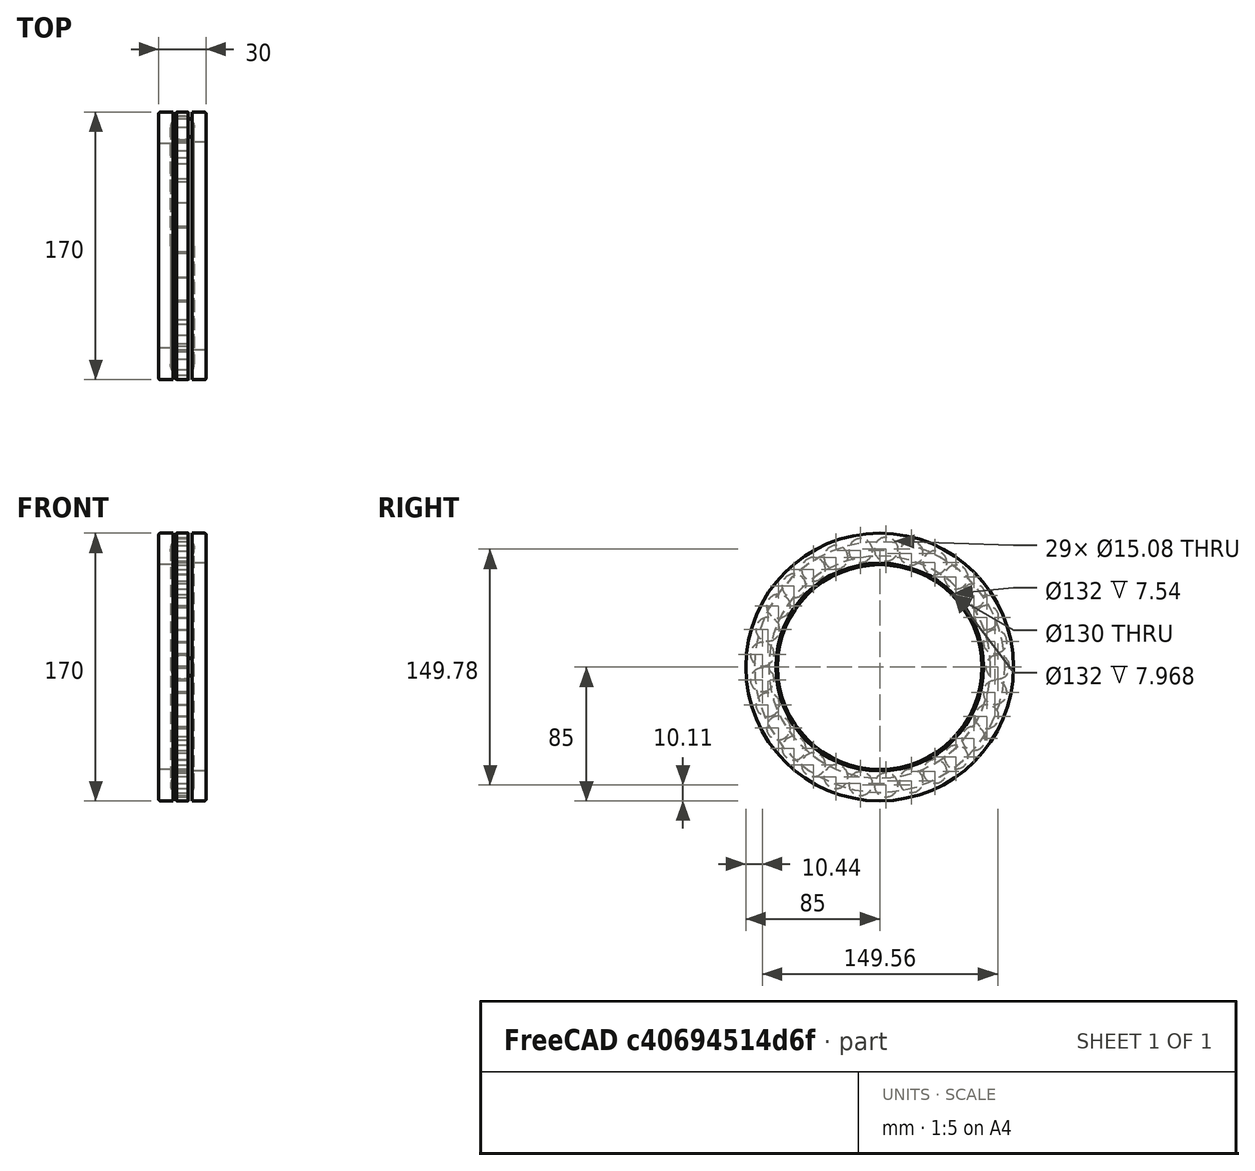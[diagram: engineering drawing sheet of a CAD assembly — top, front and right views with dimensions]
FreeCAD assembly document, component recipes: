
FREECAD ASSEMBLY — COMPONENT RECIPES ("lozysko 51126")

This assembly document has 28 components, labeled P0..P27 below (a component is one placed body or linked part). 0 of them carry a construction recipe — the FreeCAD feature program that regenerates the part from scratch, quoted from this document or its linked companion documents; the rest are supplied as boundary geometry only. No exploded tour is included for this assembly.
COMPONENT P0 — geometry summary ("_51126_PART005"; no construction recipe available for this part):
  bounding box: 15.1 x 15.1 x 15.1 mm
  tessellated surface: 8,032 triangles
  volume: 1796 mm^3 (52% of its bounding box)
  symmetry: revolution-symmetric about the x axis through its bounding-box center; revolution-symmetric about the y axis through its bounding-box center; revolution-symmetric about the z axis through its bounding-box center; mirror-symmetric across its x mid-plane, y mid-plane, z mid-plane
COMPONENT P1 — geometry summary ("_51126_PART006"; no construction recipe available for this part):
  bounding box: 15.1 x 15.1 x 15.1 mm
  tessellated surface: 8,032 triangles
  volume: 1796 mm^3 (52% of its bounding box)
  symmetry: revolution-symmetric about the x axis through its bounding-box center; revolution-symmetric about the y axis through its bounding-box center; revolution-symmetric about the z axis through its bounding-box center; mirror-symmetric across its x mid-plane, y mid-plane, z mid-plane
COMPONENT P2 — geometry summary ("_51126_PART007"; no construction recipe available for this part):
  bounding box: 15.1 x 15.1 x 15.1 mm
  tessellated surface: 8,032 triangles
  volume: 1796 mm^3 (52% of its bounding box)
  symmetry: revolution-symmetric about the x axis through its bounding-box center; revolution-symmetric about the y axis through its bounding-box center; revolution-symmetric about the z axis through its bounding-box center; mirror-symmetric across its x mid-plane, y mid-plane, z mid-plane
COMPONENT P3 — geometry summary ("_51126_PART008"; no construction recipe available for this part):
  bounding box: 15.1 x 15.1 x 15.1 mm
  tessellated surface: 8,032 triangles
  volume: 1796 mm^3 (52% of its bounding box)
  symmetry: revolution-symmetric about the x axis through its bounding-box center; revolution-symmetric about the y axis through its bounding-box center; revolution-symmetric about the z axis through its bounding-box center; mirror-symmetric across its x mid-plane, y mid-plane, z mid-plane
COMPONENT P4 — geometry summary ("_51126_PART009"; no construction recipe available for this part):
  bounding box: 15.1 x 15.1 x 15.1 mm
  tessellated surface: 8,032 triangles
  volume: 1796 mm^3 (52% of its bounding box)
  symmetry: revolution-symmetric about the x axis through its bounding-box center; revolution-symmetric about the y axis through its bounding-box center; revolution-symmetric about the z axis through its bounding-box center; mirror-symmetric across its x mid-plane, y mid-plane, z mid-plane
COMPONENT P5 — geometry summary ("_51126_PART010"; no construction recipe available for this part):
  bounding box: 15.1 x 15.1 x 15.1 mm
  tessellated surface: 8,032 triangles
  volume: 1796 mm^3 (52% of its bounding box)
  symmetry: revolution-symmetric about the x axis through its bounding-box center; revolution-symmetric about the y axis through its bounding-box center; revolution-symmetric about the z axis through its bounding-box center; mirror-symmetric across its x mid-plane, y mid-plane, z mid-plane
COMPONENT P6 — geometry summary ("_51126_PART011"; no construction recipe available for this part):
  bounding box: 15.1 x 15.1 x 15.1 mm
  tessellated surface: 8,032 triangles
  volume: 1796 mm^3 (52% of its bounding box)
  symmetry: revolution-symmetric about the x axis through its bounding-box center; revolution-symmetric about the y axis through its bounding-box center; revolution-symmetric about the z axis through its bounding-box center; mirror-symmetric across its x mid-plane, y mid-plane, z mid-plane
COMPONENT P7 — geometry summary ("_51126_PART012"; no construction recipe available for this part):
  bounding box: 15.1 x 15.1 x 15.1 mm
  tessellated surface: 8,032 triangles
  volume: 1796 mm^3 (52% of its bounding box)
  symmetry: revolution-symmetric about the x axis through its bounding-box center; revolution-symmetric about the y axis through its bounding-box center; revolution-symmetric about the z axis through its bounding-box center; mirror-symmetric across its x mid-plane, y mid-plane, z mid-plane
COMPONENT P8 — geometry summary ("_51126_PART013"; no construction recipe available for this part):
  bounding box: 15.1 x 15.1 x 15.1 mm
  tessellated surface: 8,032 triangles
  volume: 1796 mm^3 (52% of its bounding box)
  symmetry: revolution-symmetric about the x axis through its bounding-box center; revolution-symmetric about the y axis through its bounding-box center; revolution-symmetric about the z axis through its bounding-box center; mirror-symmetric across its x mid-plane, y mid-plane, z mid-plane
COMPONENT P9 — geometry summary ("_51126_PART014"; no construction recipe available for this part):
  bounding box: 15.1 x 15.1 x 15.1 mm
  tessellated surface: 8,032 triangles
  volume: 1796 mm^3 (52% of its bounding box)
  symmetry: revolution-symmetric about the x axis through its bounding-box center; revolution-symmetric about the y axis through its bounding-box center; revolution-symmetric about the z axis through its bounding-box center; mirror-symmetric across its x mid-plane, y mid-plane, z mid-plane
COMPONENT P10 — geometry summary ("_51126_PART015"; no construction recipe available for this part):
  bounding box: 15.1 x 15.1 x 15.1 mm
  tessellated surface: 8,032 triangles
  volume: 1796 mm^3 (52% of its bounding box)
  symmetry: revolution-symmetric about the x axis through its bounding-box center; revolution-symmetric about the y axis through its bounding-box center; revolution-symmetric about the z axis through its bounding-box center; mirror-symmetric across its x mid-plane, y mid-plane, z mid-plane
COMPONENT P11 — geometry summary ("_51126_PART016"; no construction recipe available for this part):
  bounding box: 15.1 x 15.1 x 15.1 mm
  tessellated surface: 8,032 triangles
  volume: 1796 mm^3 (52% of its bounding box)
  symmetry: revolution-symmetric about the x axis through its bounding-box center; revolution-symmetric about the y axis through its bounding-box center; revolution-symmetric about the z axis through its bounding-box center; mirror-symmetric across its x mid-plane, y mid-plane, z mid-plane
COMPONENT P12 — geometry summary ("_51126_PART017"; no construction recipe available for this part):
  bounding box: 15.1 x 15.1 x 15.1 mm
  tessellated surface: 8,032 triangles
  volume: 1796 mm^3 (52% of its bounding box)
  symmetry: revolution-symmetric about the x axis through its bounding-box center; revolution-symmetric about the y axis through its bounding-box center; revolution-symmetric about the z axis through its bounding-box center; mirror-symmetric across its x mid-plane, y mid-plane, z mid-plane
COMPONENT P13 — geometry summary ("_51126_PART018"; no construction recipe available for this part):
  bounding box: 15.1 x 15.1 x 15.1 mm
  tessellated surface: 8,032 triangles
  volume: 1796 mm^3 (52% of its bounding box)
  symmetry: revolution-symmetric about the x axis through its bounding-box center; revolution-symmetric about the y axis through its bounding-box center; revolution-symmetric about the z axis through its bounding-box center; mirror-symmetric across its x mid-plane, y mid-plane, z mid-plane
COMPONENT P14 — geometry summary ("_51126_PART019"; no construction recipe available for this part):
  bounding box: 15.1 x 15.1 x 15.1 mm
  tessellated surface: 8,032 triangles
  volume: 1796 mm^3 (52% of its bounding box)
  symmetry: revolution-symmetric about the x axis through its bounding-box center; revolution-symmetric about the y axis through its bounding-box center; revolution-symmetric about the z axis through its bounding-box center; mirror-symmetric across its x mid-plane, y mid-plane, z mid-plane
COMPONENT P15 — geometry summary ("_51126_PART020"; no construction recipe available for this part):
  bounding box: 15.1 x 15.1 x 15.1 mm
  tessellated surface: 8,032 triangles
  volume: 1796 mm^3 (52% of its bounding box)
  symmetry: revolution-symmetric about the x axis through its bounding-box center; revolution-symmetric about the y axis through its bounding-box center; revolution-symmetric about the z axis through its bounding-box center; mirror-symmetric across its x mid-plane, y mid-plane, z mid-plane
COMPONENT P16 — geometry summary ("_51126_PART021"; no construction recipe available for this part):
  bounding box: 15.1 x 15.1 x 15.1 mm
  tessellated surface: 8,032 triangles
  volume: 1796 mm^3 (52% of its bounding box)
  symmetry: revolution-symmetric about the x axis through its bounding-box center; revolution-symmetric about the y axis through its bounding-box center; revolution-symmetric about the z axis through its bounding-box center; mirror-symmetric across its x mid-plane, y mid-plane, z mid-plane
COMPONENT P17 — geometry summary ("_51126_PART022"; no construction recipe available for this part):
  bounding box: 15.1 x 15.1 x 15.1 mm
  tessellated surface: 8,032 triangles
  volume: 1796 mm^3 (52% of its bounding box)
  symmetry: revolution-symmetric about the x axis through its bounding-box center; revolution-symmetric about the y axis through its bounding-box center; revolution-symmetric about the z axis through its bounding-box center; mirror-symmetric across its x mid-plane, y mid-plane, z mid-plane
COMPONENT P18 — geometry summary ("_51126_PART023"; no construction recipe available for this part):
  bounding box: 15.1 x 15.1 x 15.1 mm
  tessellated surface: 8,032 triangles
  volume: 1796 mm^3 (52% of its bounding box)
  symmetry: revolution-symmetric about the x axis through its bounding-box center; revolution-symmetric about the y axis through its bounding-box center; revolution-symmetric about the z axis through its bounding-box center; mirror-symmetric across its x mid-plane, y mid-plane, z mid-plane
COMPONENT P19 — geometry summary ("_51126_PART024"; no construction recipe available for this part):
  bounding box: 15.1 x 15.1 x 15.1 mm
  tessellated surface: 8,032 triangles
  volume: 1796 mm^3 (52% of its bounding box)
  symmetry: revolution-symmetric about the x axis through its bounding-box center; revolution-symmetric about the y axis through its bounding-box center; revolution-symmetric about the z axis through its bounding-box center; mirror-symmetric across its x mid-plane, y mid-plane, z mid-plane
COMPONENT P20 — geometry summary ("_51126_PART025"; no construction recipe available for this part):
  bounding box: 15.1 x 15.1 x 15.1 mm
  tessellated surface: 8,032 triangles
  volume: 1796 mm^3 (52% of its bounding box)
  symmetry: revolution-symmetric about the x axis through its bounding-box center; revolution-symmetric about the y axis through its bounding-box center; revolution-symmetric about the z axis through its bounding-box center; mirror-symmetric across its x mid-plane, y mid-plane, z mid-plane
COMPONENT P21 — geometry summary ("_51126_PART026"; no construction recipe available for this part):
  bounding box: 15.1 x 15.1 x 15.1 mm
  tessellated surface: 8,032 triangles
  volume: 1796 mm^3 (52% of its bounding box)
  symmetry: revolution-symmetric about the x axis through its bounding-box center; revolution-symmetric about the y axis through its bounding-box center; revolution-symmetric about the z axis through its bounding-box center; mirror-symmetric across its x mid-plane, y mid-plane, z mid-plane
COMPONENT P22 — geometry summary ("_51126_PART027"; no construction recipe available for this part):
  bounding box: 15.1 x 15.1 x 15.1 mm
  tessellated surface: 8,032 triangles
  volume: 1796 mm^3 (52% of its bounding box)
  symmetry: revolution-symmetric about the x axis through its bounding-box center; revolution-symmetric about the y axis through its bounding-box center; revolution-symmetric about the z axis through its bounding-box center; mirror-symmetric across its x mid-plane, y mid-plane, z mid-plane
COMPONENT P23 — geometry summary ("_51126_PART028"; no construction recipe available for this part):
  bounding box: 15.1 x 15.1 x 15.1 mm
  tessellated surface: 8,032 triangles
  volume: 1796 mm^3 (52% of its bounding box)
  symmetry: revolution-symmetric about the x axis through its bounding-box center; revolution-symmetric about the y axis through its bounding-box center; revolution-symmetric about the z axis through its bounding-box center; mirror-symmetric across its x mid-plane, y mid-plane, z mid-plane
COMPONENT P24 — geometry summary ("_51126_PART029"; no construction recipe available for this part):
  bounding box: 15.1 x 15.1 x 15.1 mm
  tessellated surface: 8,032 triangles
  volume: 1796 mm^3 (52% of its bounding box)
  symmetry: revolution-symmetric about the x axis through its bounding-box center; revolution-symmetric about the y axis through its bounding-box center; revolution-symmetric about the z axis through its bounding-box center; mirror-symmetric across its x mid-plane, y mid-plane, z mid-plane
COMPONENT P25 — geometry summary ("_51126_PART030"; no construction recipe available for this part):
  bounding box: 15.1 x 15.1 x 15.1 mm
  tessellated surface: 8,032 triangles
  volume: 1796 mm^3 (52% of its bounding box)
  symmetry: revolution-symmetric about the x axis through its bounding-box center; revolution-symmetric about the y axis through its bounding-box center; revolution-symmetric about the z axis through its bounding-box center; mirror-symmetric across its x mid-plane, y mid-plane, z mid-plane
COMPONENT P26 — geometry summary ("_51126_PART031"; no construction recipe available for this part):
  bounding box: 15.1 x 15.1 x 15.1 mm
  tessellated surface: 8,032 triangles
  volume: 1796 mm^3 (52% of its bounding box)
  symmetry: revolution-symmetric about the x axis through its bounding-box center; revolution-symmetric about the y axis through its bounding-box center; revolution-symmetric about the z axis through its bounding-box center; mirror-symmetric across its x mid-plane, y mid-plane, z mid-plane
COMPONENT P27 — geometry summary ("_51126_PART032"; no construction recipe available for this part):
  bounding box: 15.1 x 15.1 x 15.1 mm
  tessellated surface: 8,032 triangles
  volume: 1796 mm^3 (52% of its bounding box)
  symmetry: revolution-symmetric about the x axis through its bounding-box center; revolution-symmetric about the y axis through its bounding-box center; revolution-symmetric about the z axis through its bounding-box center; mirror-symmetric across its x mid-plane, y mid-plane, z mid-plane
PROVENANCE & LICENSES
A FreeCAD (.FCStd) document from a public repository crawl; recipes are the document's own serialized feature recipes (and, for linked parts, companion documents' recipes).
License: bsd.
